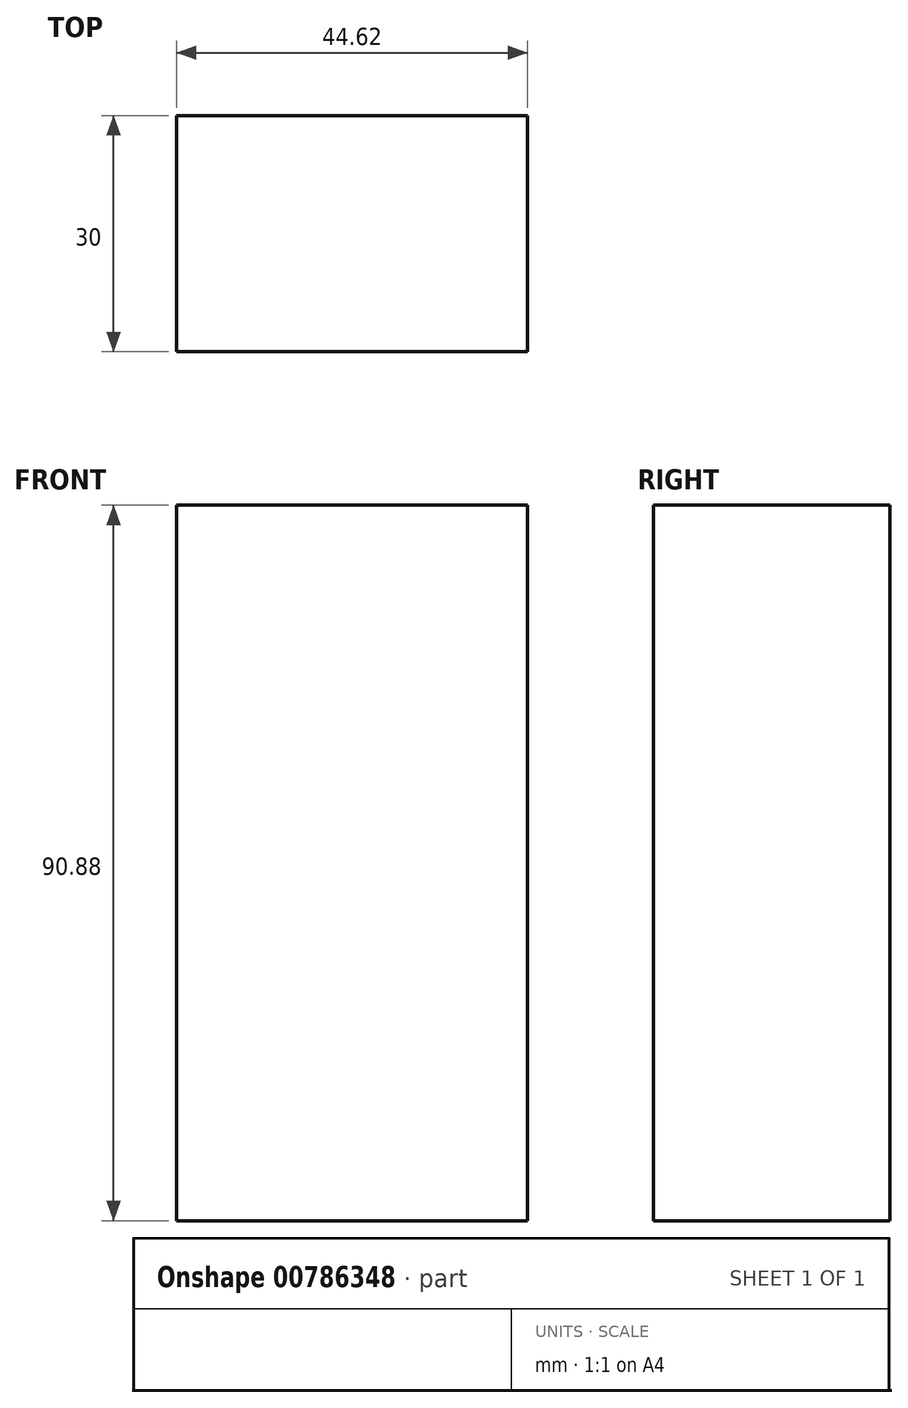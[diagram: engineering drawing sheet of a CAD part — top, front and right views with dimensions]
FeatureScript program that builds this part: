
annotation { "Feature Type Name" : "Feature", "Feature Type Description" : "" }
export const myFeature = defineFeature(function(context is Context, id is Id, definition is map)
    precondition{}
    {
        {
            var Q0;
            Q0=qCreatedBy(makeId("Front.planeOp"),FACE);
            var sketch = newSketch(context, id + "F0", { "sketchPlane" : qUnion([Q0])});
            skLineSegment(sketch, "E0.bottom", {"start": v(-22.31, 45.44) * mm, "end": v(22.31, 45.44) * mm});
            skLineSegment(sketch, "E0.top", {"start": v(-22.31, -45.44) * mm, "end": v(22.31, -45.44) * mm});
            skLineSegment(sketch, "E0.left", {"start": v(-22.31, 45.44) * mm, "end": v(-22.31, -45.44) * mm});
            skLineSegment(sketch, "E0.right", {"start": v(22.31, 45.44) * mm, "end": v(22.31, -45.44) * mm});
            skPoint(sketch, "E0.middle", {"position": v(0, 0) * mm});
            skSolve(sketch);
        }
        {
            var Q0;
            Q0=makeQuery(id+"F0.imprint","IMPRINT",FACE,{"disambiguationData":[TD([[makeQuery(id+"F0.imprint","IMPRINT",EDGE,{"derivedFrom":sQuery(id+"F0.wireOp",EDGE,"E0.bottom")}),-1.0]])]});
            extrude(context, id + "F1", {"entities" : qUnion([Q0]), "depth" : 30 * mm, "offsetDistance" : 25 * mm});
        }
    });
